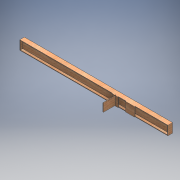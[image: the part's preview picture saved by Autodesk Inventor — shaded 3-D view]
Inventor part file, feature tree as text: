
AUTODESK INVENTOR PART (.ipt)
format: ipt  version: 2016 (Build 200138000, 138)  size: 176,640 bytes
history: native  units: mm
features: extrude x4, sketch x4
ambient origin geometry x8: Origin, YZ Plane, XZ Plane, XY Plane, X Axis, Y Axis, Z Axis, Center Point
bodies: Solid1 (feature_tree)
feature tree (8):
  extrude  "Extrusion1"  Depth=50.0mm
  extrude  "Extrusion2"  Depth=803.0mm
  extrude  "Extrusion3"  Depth=3.0mm
  extrude  "Extrusion4"  Depth=3.0mm
  sketch  "Sketch1"  dims[d0=809.0mm d1=50.0mm]
  sketch  "Sketch2"  dims[d2=3.0mm d3=0.0mm d4=803.0mm]
  sketch  "Sketch3"  dims[d5=44.0mm d6=3.0mm]
  sketch  "Sketch4"  dims[d7=3.0mm d8=3.0mm d9=600.0mm d10=12.5mm d11=12.5mm d12=0.0mm d13=0.0mm d14=50.0mm d15=23.5mm d16=3.0mm d17=0.0mm d18=15.0mm d19=40.0mm d20=3.0mm d21=44.0mm d22=80.0mm d23=0.0mm d24=3.0mm d25=15.0mm d26=50.0mm]
